FCSTD DOCUMENT  (FreeCAD 0.19R24291 (Git))
Label: prblm 14 ortho
License: All rights reserved
LicenseURL: http://en.wikipedia.org/wiki/All_rights_reserved
objects: Part::Part2DObjectPython×7
note: 7 computed .brp shape members not serialized (recipe doc carries the construction recipe); baked Part::Feature solids carry a one-line shape summary decoded from their .brp

FEATURE [Part::Part2DObjectPython] Line  # Draft 2D object (typed FeaturePython)
  Area = 0
  ChamferSize = 0
  Closed = false
  End = (600,3.67e-14,0)
  FilletRadius = 0
  Length = 600
  MakeFace = false
  Points = (2) [(0,0,0),(600,1.83697e-14,0)]
  Start = (0,0,0)
  Subdivisions = 0
FEATURE [Part::Part2DObjectPython] Line001  # Draft 2D object (typed FeaturePython)
  Area = 0
  ChamferSize = 0
  Closed = false
  End = (0,225,0)
  FilletRadius = 0
  Length = 225
  MakeFace = false
  Points = (2) [(0,0,0),(6.88864e-15,225,0)]
  Start = (0,0,0)
  Subdivisions = 0
FEATURE [Part::Part2DObjectPython] Line002  # Draft 2D object (typed FeaturePython)
  Area = 0
  ChamferSize = 0
  Closed = false
  End = (600,225,0)
  FilletRadius = 0
  Length = 225
  MakeFace = false
  Points = (2) [(600,0,0),(600,225,0)]
  Start = (600,0,0)
  Subdivisions = 0
FEATURE [Part::Part2DObjectPython] Line003  # Draft 2D object (typed FeaturePython)
  Area = 0
  ChamferSize = 0
  Closed = false
  End = (600,225,0)
  FilletRadius = 0
  Length = 600
  MakeFace = false
  Points = (2) [(-1.37773e-14,225,0),(600,225,0)]
  Start = (-1.38e-14,225,0)
  Subdivisions = 0
FEATURE [Part::Part2DObjectPython] Line004  # Draft 2D object (typed FeaturePython)
  Area = 0
  ChamferSize = 0
  Closed = false
  End = (300,0,0)
  FilletRadius = 0
  Length = 450
  MakeFace = false
  Points = (2) [(300,450,0),(300,0,0)]
  Start = (300,450,0)
  Subdivisions = 0
FEATURE [Part::Part2DObjectPython] Line005  # Draft 2D object (typed FeaturePython)
  Area = 0
  ChamferSize = 0
  Closed = false
  End = (350,0,0)
  FilletRadius = 0
  Length = 450
  MakeFace = false
  Points = (2) [(350,450,0),(350,0,0)]
  Start = (350,450,0)
  Subdivisions = 0
FEATURE [Part::Part2DObjectPython] Line006  # Draft 2D object (typed FeaturePython)
  Area = 0
  ChamferSize = 0
  Closed = false
  End = (550,0,0)
  FilletRadius = 0
  Length = 450
  MakeFace = false
  Points = (2) [(550,450,0),(550,0,0)]
  Start = (550,450,0)
  Subdivisions = 0
